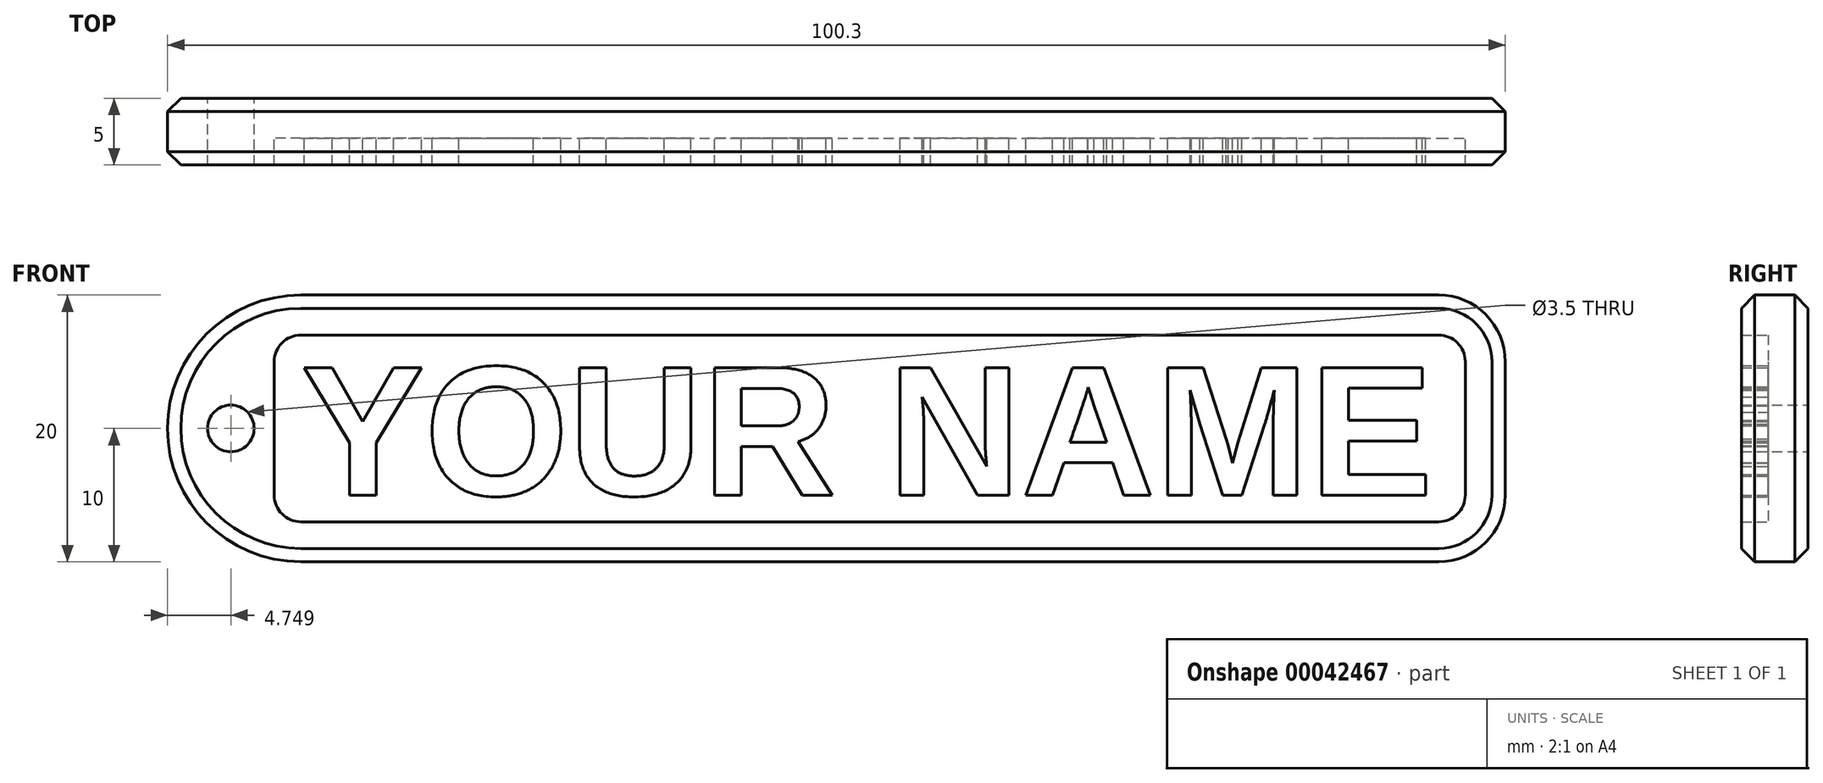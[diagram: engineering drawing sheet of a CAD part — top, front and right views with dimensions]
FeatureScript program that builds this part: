
annotation { "Feature Type Name" : "Feature", "Feature Type Description" : "" }
export const myFeature = defineFeature(function(context is Context, id is Id, definition is map)
    precondition{}
    {
        {
            var Q0;
            Q0=qCreatedBy(makeId("Front.planeOp"),FACE);
            var sketch = newSketch(context, id + "F0", { "sketchPlane" : qUnion([Q0])});
            skText(sketch, "E0", { "text": "YOUR NAME", "fontName": "Arimo-Bold.ttf"});
            const initialGuessF0  = {"E0": [-0.04265, -0.005, 1, 0, 0.01]};
            skSetInitialGuess(sketch, initialGuessF0);
            skSolve(sketch);
        }
        {
            var Q0;
            Q0 = qSketchRegion(id + "F0", true);
            extrude(context, id + "F1", {"entities" : qUnion([Q0]), "depth" : 5 * mm});
        }
        {
            var Q0;
            Q0=qCreatedBy(makeId("Front.planeOp"),FACE);
            var sketch = newSketch(context, id + "F2", { "sketchPlane" : qUnion([Q0])});
            skLineSegment(sketch, "E1.bottom", {"start": v(-42.65, 10) * mm, "end": v(42.65, 10) * mm});
            skLineSegment(sketch, "E1.top", {"start": v(-42.65, -10) * mm, "end": v(42.65, -10) * mm});
            skLineSegment(sketch, "E1.left", {"start": v(-47.65, 5) * mm, "end": v(-47.65, -5) * mm, "construction": true});
            skLineSegment(sketch, "E1.right", {"start": v(47.65, 5) * mm, "end": v(47.65, -5) * mm});
            skLineSegment(sketch, "E2", {"start": v(-47.65, 10) * mm, "end": v(47.65, -10) * mm, "construction": true});
            skPoint(sketch, "E3.visualSharp", {"position": v(-47.65, 10) * mm});
            skArc(sketch, "E3.filletArc", {"start": v(-42.65, 10) * mm, "mid": v(-46.19, 8.54) * mm, "end": v(-47.65, 5) * mm, "construction": true});
            skPoint(sketch, "E4.visualSharp", {"position": v(-47.65, -10) * mm});
            skArc(sketch, "E4.filletArc", {"start": v(-47.65, -5) * mm, "mid": v(-46.19, -8.54) * mm, "end": v(-42.65, -10) * mm, "construction": true});
            skPoint(sketch, "E5.visualSharp", {"position": v(47.65, 10) * mm});
            skArc(sketch, "E5.filletArc", {"start": v(47.65, 5) * mm, "mid": v(46.19, 8.54) * mm, "end": v(42.65, 10) * mm});
            skPoint(sketch, "E6.visualSharp", {"position": v(47.65, -10) * mm});
            skArc(sketch, "E6.filletArc", {"start": v(42.65, -10) * mm, "mid": v(46.19, -8.54) * mm, "end": v(47.65, -5) * mm});
            skLineSegment(sketch, "E7.0", {"start": v(-42.65, 7) * mm, "end": v(42.65, 7) * mm});
            skLineSegment(sketch, "E7.1", {"start": v(-44.65, 5) * mm, "end": v(-44.65, -5) * mm});
            skLineSegment(sketch, "E7.2", {"start": v(-42.65, -7) * mm, "end": v(42.65, -7) * mm});
            skLineSegment(sketch, "E7.3", {"start": v(44.65, 5) * mm, "end": v(44.65, -5) * mm});
            skPoint(sketch, "E8.visualSharp", {"position": v(-44.65, 7) * mm});
            skArc(sketch, "E8.filletArc", {"start": v(-42.65, 7) * mm, "mid": v(-44.07, 6.41) * mm, "end": v(-44.65, 5) * mm});
            skPoint(sketch, "E9.visualSharp", {"position": v(44.65, 7) * mm});
            skArc(sketch, "E9.filletArc", {"start": v(44.65, 5) * mm, "mid": v(44.07, 6.41) * mm, "end": v(42.65, 7) * mm});
            skPoint(sketch, "E10.visualSharp", {"position": v(44.65, -7) * mm});
            skArc(sketch, "E10.filletArc", {"start": v(42.65, -7) * mm, "mid": v(44.07, -6.41) * mm, "end": v(44.65, -5) * mm});
            skPoint(sketch, "E11.visualSharp", {"position": v(-44.65, -7) * mm});
            skArc(sketch, "E11.filletArc", {"start": v(-44.65, -5) * mm, "mid": v(-44.07, -6.41) * mm, "end": v(-42.65, -7) * mm});
            skArc(sketch, "E12", {"start": v(-42.65, 10) * mm, "mid": v(-52.65, 0) * mm, "end": v(-42.65, -10) * mm});
            skCircle(sketch, "E13", {"center": v(-47.9, 0) * mm, "radius": 1.75 * mm});
            skPoint(sketch, "E13.centerSnap0", {"position": v(-47.65, 0) * mm});
            skSolve(sketch);
        }
        {
            var Q0;
            Q0 = qSketchRegion(id + "F2", true);
            var Q1;
            Q1=makeQuery(id+"F1.opExtrude","CAP_FACE",FACE,{"disambiguationData":[OSD([sQuery(id+"F0.wireOp",EDGE,"E0.sketch_text.stroke-0"),sQuery(id+"F0.wireOp",EDGE,"E0.sketch_text.stroke-1"),sQuery(id+"F0.wireOp",EDGE,"E0.sketch_text.stroke-2"),sQuery(id+"F0.wireOp",EDGE,"E0.sketch_text.stroke-3"),sQuery(id+"F0.wireOp",EDGE,"E0.sketch_text.stroke-4"),sQuery(id+"F0.wireOp",EDGE,"E0.sketch_text.stroke-5"),sQuery(id+"F0.wireOp",EDGE,"E0.sketch_text.stroke-6"),sQuery(id+"F0.wireOp",EDGE,"E0.sketch_text.stroke-7"),sQuery(id+"F0.wireOp",EDGE,"E0.sketch_text.stroke-8"),sQuery(id+"F0.wireOp",EDGE,"E0.sketch_text.stroke-9"),sQuery(id+"F0.wireOp",EDGE,"E0.sketch_text.stroke-10"),sQuery(id+"F0.wireOp",EDGE,"E0.sketch_text.stroke-11")])],"isStart":false});
            extrude(context, id + "F3", {"entities" : qUnion([Q0]), "endBound" : BoundingType.UP_TO_SURFACE, "endBoundEntityFace" : qUnion([Q1]), "offsetDistance" : 25 * mm, "depth" : 25 * mm});
        }
        {
            var Q0;
            Q0=qCreatedBy(makeId("Front.planeOp"),FACE);
            var sketch = newSketch(context, id + "F4", { "sketchPlane" : qUnion([Q0])});
            skLineSegment(sketch, "E14.0", {"start": v(-42.65, 7) * mm, "end": v(42.65, 7) * mm});
            skArc(sketch, "E14.1", {"start": v(-42.65, 7) * mm, "mid": v(-44.07, 6.41) * mm, "end": v(-44.65, 5) * mm});
            skLineSegment(sketch, "E14.2", {"start": v(-44.65, 5) * mm, "end": v(-44.65, -5) * mm});
            skArc(sketch, "E14.3", {"start": v(-44.65, -5) * mm, "mid": v(-44.07, -6.41) * mm, "end": v(-42.65, -7) * mm});
            skLineSegment(sketch, "E14.4", {"start": v(-42.65, -7) * mm, "end": v(42.65, -7) * mm});
            skArc(sketch, "E14.5", {"start": v(42.65, -7) * mm, "mid": v(44.07, -6.41) * mm, "end": v(44.65, -5) * mm});
            skLineSegment(sketch, "E14.6", {"start": v(44.65, 5) * mm, "end": v(44.65, -5) * mm});
            skArc(sketch, "E14.7", {"start": v(44.65, 5) * mm, "mid": v(44.07, 6.41) * mm, "end": v(42.65, 7) * mm});
            skSolve(sketch);
        }
        {
            var Q0;
            Q0 = qSketchRegion(id + "F4", true);
            extrude(context, id + "F5", {"entities" : qUnion([Q0]), "operationType" : NewBodyOperationType.ADD, "depth" : 3 * mm});
        }
        {
            var Q0;
            Q0=makeQuery(id+"F3.opExtrude","CAP_EDGE",EDGE,{"disambiguationData":[OSD([sQuery(id+"F2.wireOp",EDGE,"E12")])],"isStart":true});
            var Q1;
            Q1=makeQuery(id+"F3.opExtrude","CAP_EDGE",EDGE,{"disambiguationData":[OSD([sQuery(id+"F2.wireOp",EDGE,"E12")])],"isStart":false});
            chamfer(context, id + "F6", {"entities" : qUnion([Q0, Q1]), "width" : 1 * mm, "tangentPropagation" : true});
        }
    });
